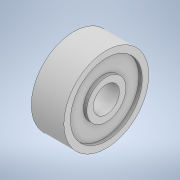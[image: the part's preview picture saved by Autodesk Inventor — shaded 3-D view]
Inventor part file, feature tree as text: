
AUTODESK INVENTOR PART (.ipt)
format: ipt  version: 2020 (Build 240168000, 168)  size: 126,976 bytes
history: native  units: mm
features: extrude x2, other x1, sketch x1
ambient origin geometry x8: Origin, YZ Plane, XZ Plane, XY Plane, X Axis, Y Axis, Z Axis, Center Point
bodies: Body1 (feature_tree)
feature tree (4):
  other  "Твердое тело1"
  sketch  "Эскиз1"
  extrude  "Выдавливание1"  Depth=4.0mm
  extrude  "Выдавливание2"  Depth=13.0mm
